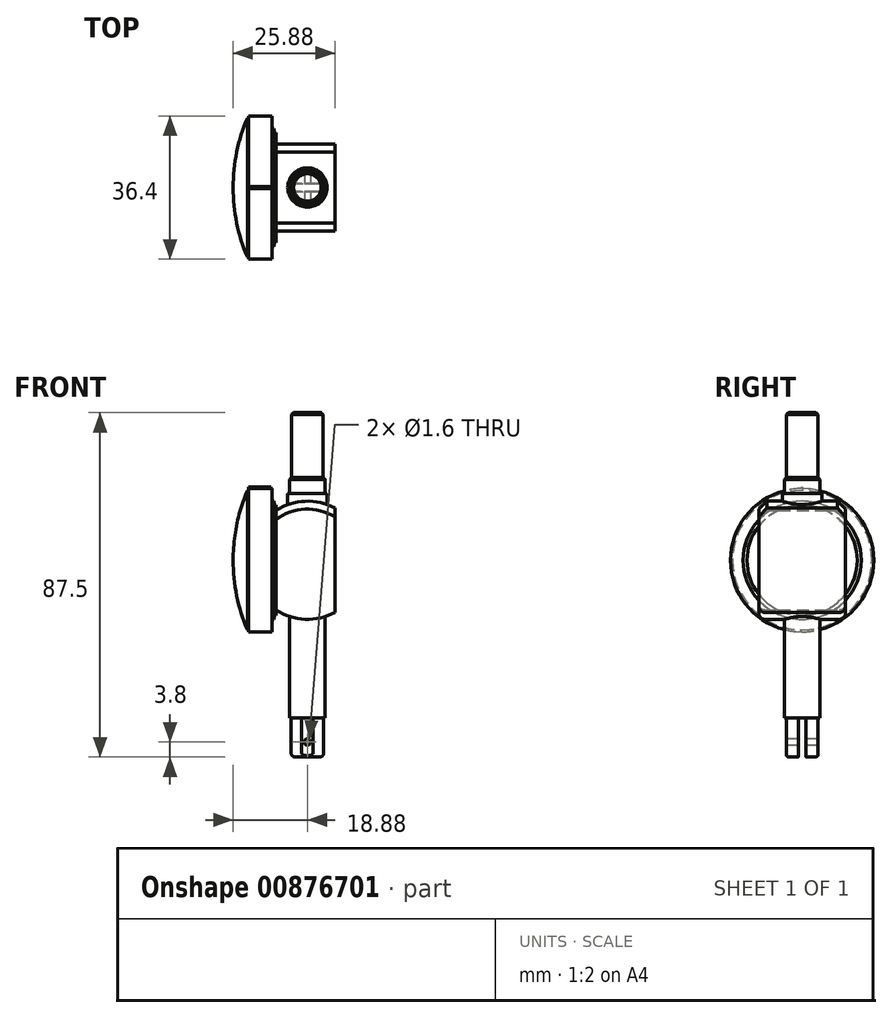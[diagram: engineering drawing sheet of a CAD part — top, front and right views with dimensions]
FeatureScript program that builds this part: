
annotation { "Feature Type Name" : "Feature", "Feature Type Description" : "" }
export const myFeature = defineFeature(function(context is Context, id is Id, definition is map)
    precondition{}
    {
        {
            var Q0;
            Q0=qCreatedBy(makeId("Front.planeOp"),FACE);
            var sketch = newSketch(context, id + "F0", { "sketchPlane" : qUnion([Q0])});
            skArc(sketch, "E0", {"start": v(7, 13.27) * mm, "mid": v(-0.58, 14.99) * mm, "end": v(-8, 12.69) * mm});
            skLineSegment(sketch, "E1", {"start": v(7, 13.27) * mm, "end": v(7, -13.27) * mm});
            skLineSegment(sketch, "E2", {"start": v(-8, 12.69) * mm, "end": v(-8, -12.69) * mm});
            skArc(sketch, "E3.trimOffspring", {"start": v(-8, -12.69) * mm, "mid": v(-0.58, -14.99) * mm, "end": v(7, -13.27) * mm});
            skSolve(sketch);
        }
        {
            var Q0;
            Q0=makeQuery(id+"F0.imprint","IMPRINT",FACE,{"disambiguationData":[TD([[makeQuery(id+"F0.imprint","IMPRINT",EDGE,{"derivedFrom":sQuery(id+"F0.wireOp",EDGE,"E0")}),1.0]])]});
            extrude(context, id + "F1", {"entities" : qUnion([Q0]), "endBound" : BoundingType.SYMMETRIC, "depth" : 22 * mm, "offsetDistance" : 25 * mm});
        }
        {
            var Q0;
            Q0=makeQuery(id+"F1.opExtrude","CAP_EDGE",EDGE,{"disambiguationData":[OSD([sQuery(id+"F0.wireOp",EDGE,"E0")])],"isStart":false});
            var Q1;
            Q1=makeQuery(id+"F1.opExtrude","CAP_EDGE",EDGE,{"disambiguationData":[OSD([sQuery(id+"F0.wireOp",EDGE,"E0")])],"isStart":true});
            chamfer(context, id + "F2", {"entities" : qUnion([Q0, Q1]), "width" : 2 * mm, "tangentPropagation" : true});
        }
        {
            var Q0;
            Q0=makeQuery(id+"F1.opExtrude","CAP_EDGE",EDGE,{"disambiguationData":[OSD([sQuery(id+"F0.wireOp",EDGE,"E3.trimOffspring")])],"isStart":false});
            var Q1;
            Q1=makeQuery(id+"F1.opExtrude","CAP_EDGE",EDGE,{"disambiguationData":[OSD([sQuery(id+"F0.wireOp",EDGE,"E3.trimOffspring")])],"isStart":true});
            fillet(context, id + "F3", {"entities" : qUnion([Q0, Q1]), "radius" : 1.5 * mm, "tangentPropagation" : true, "allowEdgeOverflow" : false});
        }
        {
            var Q0;
            Q0=qCreatedBy(makeId("Top.planeOp"),FACE);
            var sketch = newSketch(context, id + "F4", { "sketchPlane" : qUnion([Q0])});
            skCircle(sketch, "E4", {"center": v(0, 0) * mm, "radius": 5 * mm});
            skSolve(sketch);
        }
        {
            var Q0;
            Q0=qSketchRegion(id+"F4",true);
            var Q1;
            Q1 = qSketchRegion(id + "F6", true);
            extrude(context, id + "F5", {"entities" : qUnion([Q0, Q1]), "operationType" : NewBodyOperationType.ADD, "depth" : 17 * mm, "offsetDistance" : 25 * mm});
        }
        {
            var Q0;
            Q0=makeQuery(id+"F5.opExtrude","CAP_FACE",FACE,{"disambiguationData":[OSD([sQuery(id+"F4.wireOp",EDGE,"E4")])],"isStart":false});
            var sketch = newSketch(context, id + "F6", { "sketchPlane" : qUnion([Q0])});
            skCircle(sketch, "E5", {"center": v(0, 0) * mm, "radius": 4.5 * mm});
            skSolve(sketch);
        }
        {
            var Q0;
            Q0=makeQuery(id+"F6.imprint","IMPRINT",FACE,{"disambiguationData":[TD([[makeQuery(id+"F6.imprint","IMPRINT",EDGE,{"derivedFrom":sQuery(id+"F6.wireOp",EDGE,"E5")}),1.0]])]});
            extrude(context, id + "F7", {"entities" : qUnion([Q0]), "operationType" : NewBodyOperationType.ADD, "depth" : 3.5 * mm, "offsetDistance" : 25 * mm});
        }
        {
            var Q0;
            Q0=makeQuery(id+"F7.opExtrude","CAP_FACE",FACE,{"disambiguationData":[OSD([sQuery(id+"F6.wireOp",EDGE,"E5")])],"isStart":false});
            var sketch = newSketch(context, id + "F8", { "sketchPlane" : qUnion([Q0])});
            skCircle(sketch, "E6", {"center": v(0, 0) * mm, "radius": 4 * mm});
            skSolve(sketch);
        }
        {
            var Q0;
            Q0=makeQuery(id+"F8.imprint","IMPRINT",FACE,{"disambiguationData":[TD([[makeQuery(id+"F8.imprint","IMPRINT",EDGE,{"derivedFrom":sQuery(id+"F8.wireOp",EDGE,"E6")}),1.0]])]});
            var Q1;
            Q1=qSketchRegion(id+"F11",true);
            extrude(context, id + "F9", {"entities" : qUnion([Q0, Q1]), "operationType" : NewBodyOperationType.ADD, "depth" : 17 * mm, "offsetDistance" : 25 * mm});
        }
        {
            var Q0;
            Q0=makeQuery(id+"F9.opExtrude","CAP_EDGE",EDGE,{"disambiguationData":[OSD([sQuery(id+"F8.wireOp",EDGE,"E6")])],"isStart":false});
            var Q1;
            Q1=makeQuery(id+"F9.opExtrude","SWEPT_FACE",FACE,{"disambiguationData":[OSD([sQuery(id+"F8.wireOp",EDGE,"E6")])]});
            chamfer(context, id + "F10", {"entities" : qUnion([Q0, Q1]), "width" : 0.5 * mm, "tangentPropagation" : true});
        }
        {
            var Q0;
            Q0=qCreatedBy(makeId("Top.planeOp"),FACE);
            var sketch = newSketch(context, id + "F11", { "sketchPlane" : qUnion([Q0])});
            skCircle(sketch, "E7", {"center": v(0, 0) * mm, "radius": 4.5 * mm});
            skSolve(sketch);
        }
        {
            var Q0;
            Q0=qSketchRegion(id+"F11",true);
            extrude(context, id + "F12", {"entities" : qUnion([Q0]), "operationType" : NewBodyOperationType.ADD, "oppositeDirection" : true, "depth" : 40 * mm, "offsetDistance" : 25 * mm});
        }
        {
            var Q0;
            Q0=makeQuery(id+"F12.opExtrude","CAP_FACE",FACE,{"disambiguationData":[OSD([sQuery(id+"F11.wireOp",EDGE,"E7")])],"isStart":false});
            var sketch = newSketch(context, id + "F13", { "sketchPlane" : qUnion([Q0])});
            skCircle(sketch, "E8", {"center": v(0, 0) * mm, "radius": 4.25 * mm});
            skSolve(sketch);
        }
        {
            var Q0;
            Q0=makeQuery(id+"F13.imprint","IMPRINT",FACE,{"disambiguationData":[TD([[makeQuery(id+"F13.imprint","IMPRINT",EDGE,{"derivedFrom":sQuery(id+"F13.wireOp",EDGE,"E8")}),1.0]])]});
            extrude(context, id + "F14", {"entities" : qUnion([Q0]), "operationType" : NewBodyOperationType.ADD, "depth" : 10 * mm, "offsetDistance" : 25 * mm});
        }
        {
            var Q0;
            Q0=makeQuery(id+"F14.opExtrude","CAP_EDGE",EDGE,{"disambiguationData":[OSD([sQuery(id+"F13.wireOp",EDGE,"E8")])],"isStart":false});
            fillet(context, id + "F15", {"entities" : qUnion([Q0]), "radius" : 1 * mm, "tangentPropagation" : true, "allowEdgeOverflow" : false});
        }
        {
            var Q0;
            Q0=qCreatedBy(makeId("Front.planeOp"),FACE);
            var sketch = newSketch(context, id + "F16", { "sketchPlane" : qUnion([Q0])});
            skLineSegment(sketch, "E9.0", {"start": v(-8, 10.25) * mm, "end": v(-8, -10.87) * mm});
            skLineSegment(sketch, "E10", {"start": v(-8, 0) * mm, "end": v(-8, 14) * mm});
            skLineSegment(sketch, "E11", {"start": v(-8, 14) * mm, "end": v(-8.5, 14) * mm});
            skLineSegment(sketch, "E12", {"start": v(-8.5, 14) * mm, "end": v(-8.5, 15) * mm});
            skLineSegment(sketch, "E13", {"start": v(-8.5, 15) * mm, "end": v(-9, 15) * mm});
            skLineSegment(sketch, "E14", {"start": v(-9, 15) * mm, "end": v(-9, 18.2) * mm});
            skLineSegment(sketch, "E15", {"start": v(-15, 18.2) * mm, "end": v(-9, 18.2) * mm});
            skLineSegment(sketch, "E16", {"start": v(-15, 17.7) * mm, "end": v(-15.25, 17.7) * mm});
            skLineSegment(sketch, "E17", {"start": v(-15, 18.2) * mm, "end": v(-15, 17.7) * mm});
            skLineSegment(sketch, "E18", {"start": v(-8, 0) * mm, "end": v(-18.88, 0) * mm});
            skArc(sketch, "E19", {"start": v(-15.25, 17.7) * mm, "mid": v(-17.96, 9.03) * mm, "end": v(-18.88, 0) * mm});
            skSolve(sketch);
        }
        {
            var Q0;
            {var subQ0=sQuery(id+"F16.wireOp",EDGE,"E11");Q0=makeQuery(id+"F16.imprint","IMPRINT",FACE,{"disambiguationData":[TD([[makeQuery(id+"F16.imprint","IMPRINT",EDGE,{"derivedFrom":subQ0}),1.0]])]});}
            var Q1;
            Q1=sQuery(id+"F16.wireOp",EDGE,"E18");
            revolve(context, id + "F17", {"operationType" : NewBodyOperationType.ADD, "surfaceOperationType" : NewSurfaceOperationType.NEW, "entities" : qUnion([Q0]), "axis" : qUnion([Q1]), "revolveType" : RevolveType.FULL});
        }
        {
            var Q0;
            Q0=qCreatedBy(makeId("Right.planeOp"),FACE);
            var sketch = newSketch(context, id + "F18", { "sketchPlane" : qUnion([Q0])});
            skLineSegment(sketch, "E20.0", {"start": v(-4.5, -40) * mm, "end": v(4.5, -40) * mm, "construction": true});
            skLineSegment(sketch, "E21.bottom", {"start": v(-1, -40) * mm, "end": v(1, -40) * mm});
            skLineSegment(sketch, "E21.top", {"start": v(-1, -51) * mm, "end": v(1, -51) * mm});
            skLineSegment(sketch, "E21.left", {"start": v(-1, -40) * mm, "end": v(-1, -51) * mm});
            skLineSegment(sketch, "E21.right", {"start": v(1, -40) * mm, "end": v(1, -51) * mm});
            skLineSegment(sketch, "E22.bottom", {"start": v(-4, -40) * mm, "end": v(-6, -40) * mm});
            skLineSegment(sketch, "E22.top", {"start": v(-4, -51) * mm, "end": v(-6, -51) * mm});
            skLineSegment(sketch, "E22.left", {"start": v(-4, -40) * mm, "end": v(-4, -51) * mm});
            skLineSegment(sketch, "E22.right", {"start": v(-6, -40) * mm, "end": v(-6, -51) * mm});
            skLineSegment(sketch, "E23.bottom", {"start": v(4, -40) * mm, "end": v(6, -40) * mm});
            skLineSegment(sketch, "E23.top", {"start": v(4, -51) * mm, "end": v(6, -51) * mm});
            skLineSegment(sketch, "E23.left", {"start": v(4, -40) * mm, "end": v(4, -51) * mm});
            skLineSegment(sketch, "E23.right", {"start": v(6, -40) * mm, "end": v(6, -51) * mm});
            skLineSegment(sketch, "E24.0", {"start": v(3.25, -50) * mm, "end": v(-3.25, -50) * mm, "construction": true});
            skLineSegment(sketch, "E25", {"start": v(-4.5, -40) * mm, "end": v(-1, -40) * mm});
            skLineSegment(sketch, "E26", {"start": v(1, -40) * mm, "end": v(4.5, -40) * mm});
            skLineSegment(sketch, "E27", {"start": v(-4, -42.75) * mm, "end": v(-1, -42.75) * mm, "construction": true});
            skLineSegment(sketch, "E28", {"start": v(1, -45.5) * mm, "end": v(4, -45.5) * mm, "construction": true});
            skSolve(sketch);
        }
        {
            var Q0;
            Q0=qSketchRegion(id+"F18",true);
            extrude(context, id + "F19", {"entities" : qUnion([Q0]), "operationType" : NewBodyOperationType.REMOVE, "endBound" : BoundingType.SYMMETRIC, "oppositeDirection" : true, "depth" : 25 * mm, "offsetDistance" : 25 * mm});
        }
        {
            var Q0;
            Q0=makeQuery(id+"F19.boolean.opBoolean","COPY",FACE,{"derivedFrom":makeQuery(id+"F19.opExtrude","SWEPT_FACE",FACE,{"disambiguationData":[OSD([sQuery(id+"F18.wireOp",EDGE,"E22.left")])]})});
            var sketch = newSketch(context, id + "F20", { "sketchPlane" : qUnion([Q0])});
            skCircle(sketch, "E29", {"center": v(0, -46.2) * mm, "radius": 0.8 * mm});
            skLineSegment(sketch, "E30.0", {"start": v(3.1, -50) * mm, "end": v(-3.1, -50) * mm});
            skSolve(sketch);
        }
        {
            var Q0;
            Q0=makeQuery(id+"F20.imprint","IMPRINT",FACE,{"disambiguationData":[TD([[makeQuery(id+"F20.imprint","IMPRINT",EDGE,{"derivedFrom":sQuery(id+"F20.wireOp",EDGE,"E29")}),1.0]])]});
            extrude(context, id + "F21", {"entities" : qUnion([Q0]), "operationType" : NewBodyOperationType.REMOVE, "endBound" : BoundingType.THROUGH_ALL, "oppositeDirection" : true, "depth" : 25 * mm, "offsetDistance" : 25 * mm});
        }
        {
            var Q0;
            Q0=makeQuery(id+"F17.opRevolve","SWEPT_FACE",FACE,{"disambiguationData":[OSD([sQuery(id+"F16.wireOp",EDGE,"E17")])]});
            var sketch = newSketch(context, id + "F22", { "sketchPlane" : qUnion([Q0])});
            skCircle(sketch, "E31.0", {"center": v(0, 0) * mm, "radius": 18.2 * mm});
            skLineSegment(sketch, "E32", {"start": v(-0.29, 18.2) * mm, "end": v(0, 18.6) * mm});
            skLineSegment(sketch, "E33", {"start": v(0, 18.6) * mm, "end": v(0.29, 18.2) * mm});
            skSolve(sketch);
        }
        {
            var Q0;
            {var subQ0=sQuery(id+"F22.wireOp",EDGE,"E32");Q0=makeQuery(id+"F22.imprint","IMPRINT",FACE,{"disambiguationData":[TD([[makeQuery(id+"F22.imprint","IMPRINT",EDGE,{"derivedFrom":subQ0}),-1.0]])]});}
            extrude(context, id + "F23", {"entities" : qUnion([Q0]), "operationType" : NewBodyOperationType.ADD, "oppositeDirection" : true, "depth" : 5.8 * mm, "offsetDistance" : 25 * mm});
        }
    });
